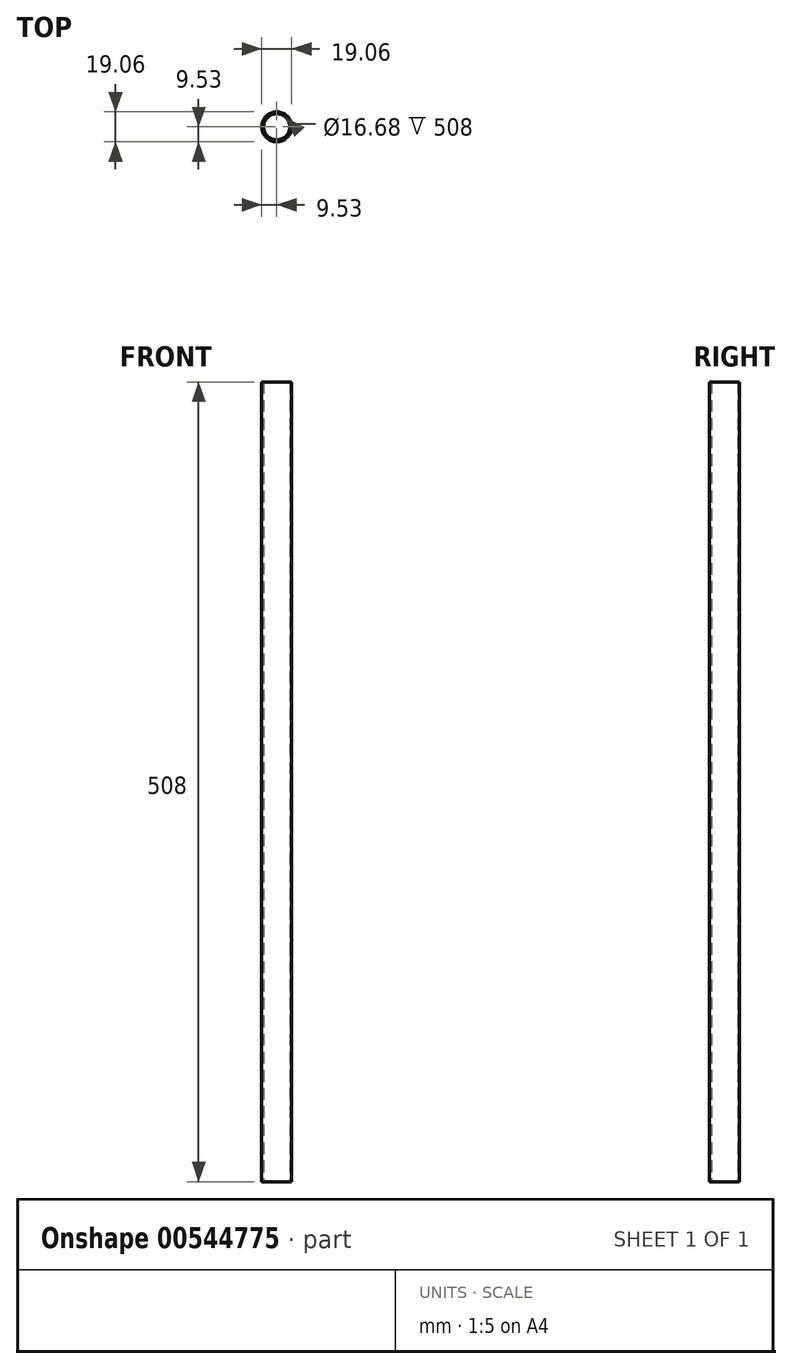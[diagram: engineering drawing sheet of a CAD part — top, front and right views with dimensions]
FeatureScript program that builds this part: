
annotation { "Feature Type Name" : "Feature", "Feature Type Description" : "" }
export const myFeature = defineFeature(function(context is Context, id is Id, definition is map)
    precondition{}
    {
        {
            var Q0;
            Q0=qCreatedBy(makeId("Top.planeOp"),FACE);
            var sketch = newSketch(context, id + "F0", { "sketchPlane" : qUnion([Q0])});
            skCircle(sketch, "E0", {"center": v(0, 0) * mm, "radius": 9.53 * mm});
            skCircle(sketch, "E1", {"center": v(0, 0) * mm, "radius": 8.34 * mm});
            skSolve(sketch);
        }
        {
            var Q0;
            Q0=makeQuery(id+"F0.imprint","IMPRINT",FACE,{"disambiguationData":[TD([[makeQuery(id+"F0.imprint","IMPRINT",EDGE,{"derivedFrom":sQuery(id+"F0.wireOp",EDGE,"E0")}),1.0]])]});
            extrude(context, id + "F1", {"entities" : qUnion([Q0]), "depth" : 508 * mm, "offsetDistance" : 25.4 * mm});
        }
    });
